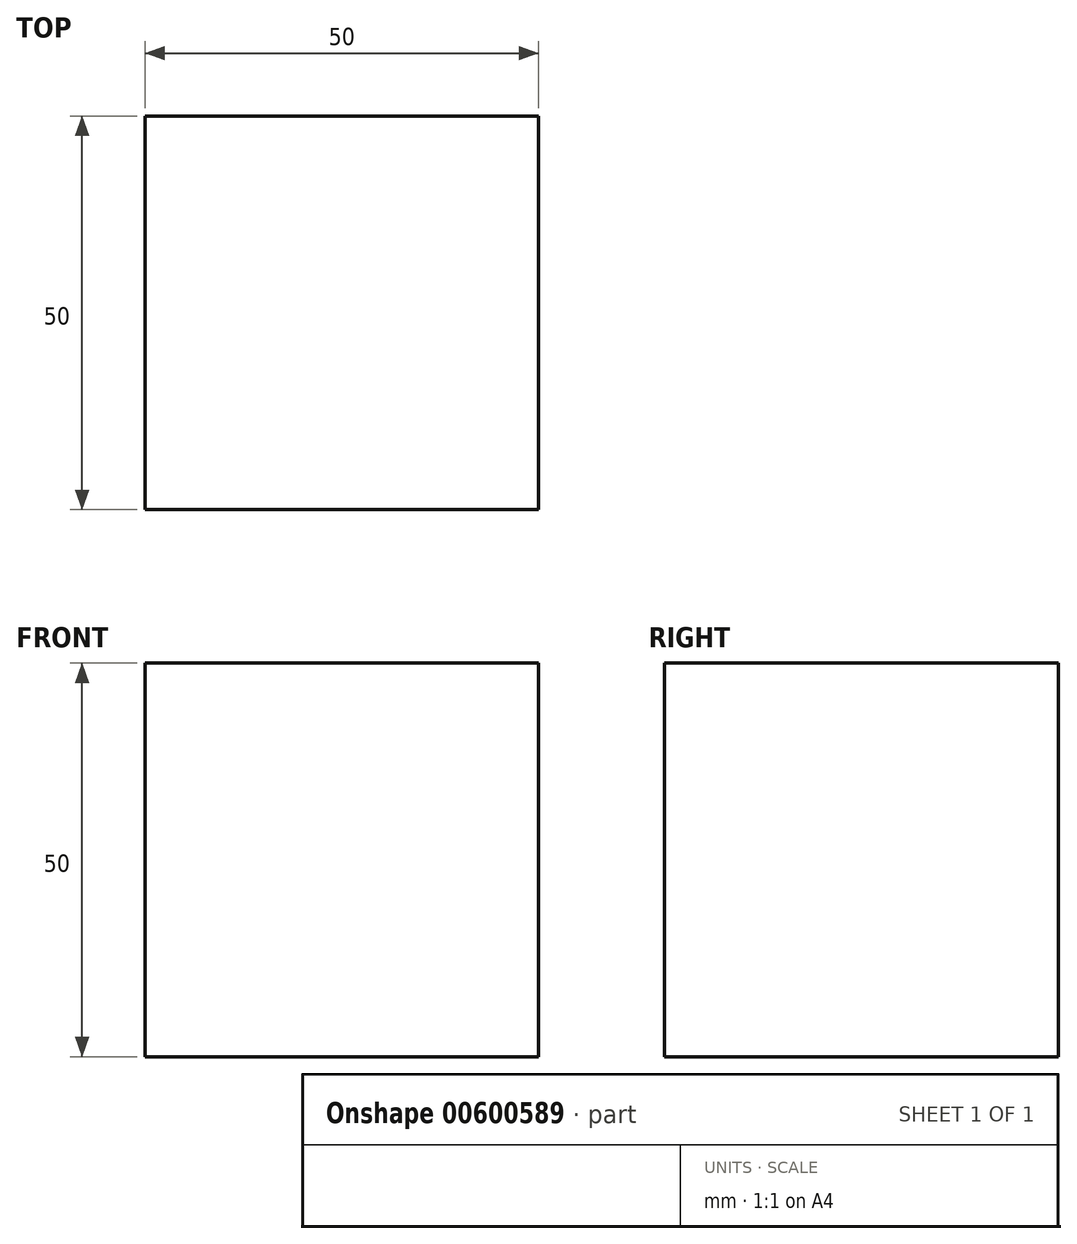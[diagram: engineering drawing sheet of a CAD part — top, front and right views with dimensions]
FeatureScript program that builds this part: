
annotation { "Feature Type Name" : "Feature", "Feature Type Description" : "" }
export const myFeature = defineFeature(function(context is Context, id is Id, definition is map)
    precondition{}
    {
        {
            var Q0;
            Q0=qCreatedBy(makeId("Top.planeOp"),FACE);
            var sketch = newSketch(context, id + "F0", { "sketchPlane" : qUnion([Q0])});
            skLineSegment(sketch, "E0.bottom", {"start": v(-25, -25) * mm, "end": v(25, -25) * mm});
            skLineSegment(sketch, "E0.top", {"start": v(-25, 25) * mm, "end": v(25, 25) * mm});
            skLineSegment(sketch, "E0.left", {"start": v(-25, -25) * mm, "end": v(-25, 25) * mm});
            skLineSegment(sketch, "E0.right", {"start": v(25, -25) * mm, "end": v(25, 25) * mm});
            skPoint(sketch, "E0.middle", {"position": v(0, 0) * mm});
            skSolve(sketch);
        }
        {
            var Q0;
            Q0=makeQuery(id+"F0.imprint","IMPRINT",FACE,{"disambiguationData":[TD([[makeQuery(id+"F0.imprint","IMPRINT",EDGE,{"derivedFrom":sQuery(id+"F0.wireOp",EDGE,"E0.bottom")}),1.0]])]});
            extrude(context, id + "F1", {"entities" : qUnion([Q0]), "depth" : 50 * mm, "offsetDistance" : 25 * mm});
        }
    });
